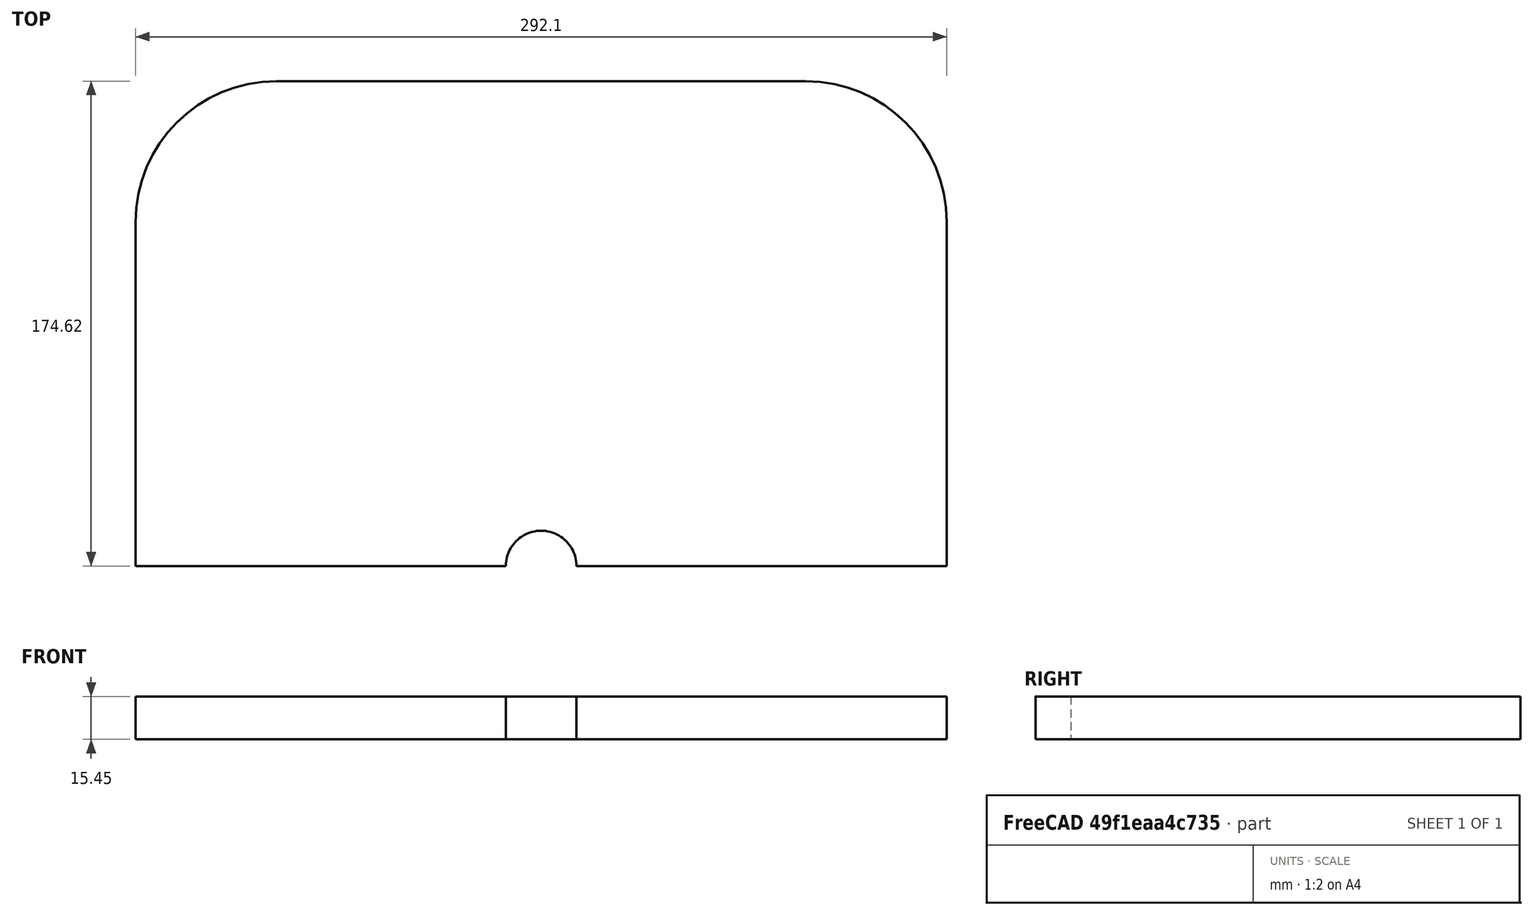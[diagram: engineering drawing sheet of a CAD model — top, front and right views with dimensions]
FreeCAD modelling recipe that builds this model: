
FCSTD DOCUMENT  (FreeCAD 1.0R39285 (Git))
Label: sink_cover
License: All rights reserved
LicenseURL: https://en.wikipedia.org/wiki/All_rights_reserved
objects: Sketcher::SketchObject×1, PartDesign::Pad×1, PartDesign::Body×1, App::Part×1
note: 6 computed .brp shape members not serialized (recipe doc carries the construction recipe); baked Part::Feature solids carry a one-line shape summary decoded from their .brp

FEATURE [Sketcher::SketchObject] Sketch
  ArcFitTolerance = 1e-06
  AttachmentSupport = -> [XY_Plane001]
  FullyConstrained = true
  MakeInternals = false
  MapMode = 5
  sketch-geometry (10):
    g0: LineSegment StartX=-146.05 StartY=36.5125 StartZ=0 EndX=-146.05 EndY=-87.3125 EndZ=0
    g1: LineSegment StartX=-146.05 StartY=-87.3125 StartZ=0 EndX=-12.7 EndY=-87.3125 EndZ=0
    g2: LineSegment StartX=146.05 StartY=-87.3075 StartZ=0 EndX=146.05 EndY=36.5125 EndZ=0
    g3: LineSegment StartX=95.25 StartY=87.3125 StartZ=0 EndX=-95.25 EndY=87.3125 EndZ=0
    g4: ArcOfCircle CenterX=-95.25 CenterY=36.5125 CenterZ=0 NormalX=0 NormalY=0 NormalZ=1 AngleXU=0 Radius=50.8 StartAngle=1.5708 EndAngle=3.14159
    g5: GeomPoint [constr] X=-146.05 Y=87.3125 Z=0
    g6: ArcOfCircle CenterX=95.25 CenterY=36.5125 CenterZ=0 NormalX=0 NormalY=0 NormalZ=1 AngleXU=0 Radius=50.8 StartAngle=0 EndAngle=1.5708
    g7: GeomPoint [constr] X=146.05 Y=87.3125 Z=0
    g8: ArcOfCircle CenterX=0 CenterY=-87.31 CenterZ=0 NormalX=0 NormalY=0 NormalZ=1 AngleXU=0 Radius=12.7 StartAngle=6.28299 EndAngle=9.42497
    g9: LineSegment StartX=12.7 StartY=-87.3125 StartZ=0 EndX=146.05 EndY=-87.3075 EndZ=0
  constraints (26):
    c: Coincident(g0,g1)
    c: Coincident(g9,g2)
    c: Vertical(g0)
    c: Vertical(g2)
    c: Horizontal(g1)
    c: Horizontal(g3)
    c: Distance(g5,g7) = 292.1
    c: Distance(g1,g5) = 174.625
    c: Symmetric(g7,g0,g-1)
    c: PointOnObject(g5,g0)
    c: PointOnObject(g5,g3)
    c: Tangent(g0,g4) = -1.5708
    c: Tangent(g3,g4) = -1.5708
    c: PointOnObject(g7,g3)
    c: PointOnObject(g7,g2)
    c: Tangent(g3,g6) = -1.5708
    c: Tangent(g2,g6) = -1.5708
    c: Radius(g4) = 50.8
    c: Radius(g6) = 50.8
    c: Diameter(g8) = 25.4
    c: Symmetric(g1,g9,g8)
    c: PointOnObject(g8,g9)
    c: Coincident(g1,g8)
    c: PointOnObject(g9,g8)
    c: DistanceY(g8,g-1) = 87.31
    c: DistanceY(g8,g1) = 0
FEATURE [PartDesign::Pad] Pad  label="SinkCover"
  Direction = (0,0,1)
  Length = 15.45
  Length2 = 10
  Profile = -> Sketch
  ReferenceAxis = -> Sketch [N_Axis]
  Refine = true
  Suppressed = false
  Type = 0
FEATURE [PartDesign::Body] Body  label="SinkCoverBody"
  AllowCompound = false
  Group = -> [Sketch,Pad]
  Origin = -> Origin001
  Tip = -> Pad
FEATURE [App::Part] Part  label="SinkCoverPart"
  Group = -> [Body]
  Origin = -> Origin
